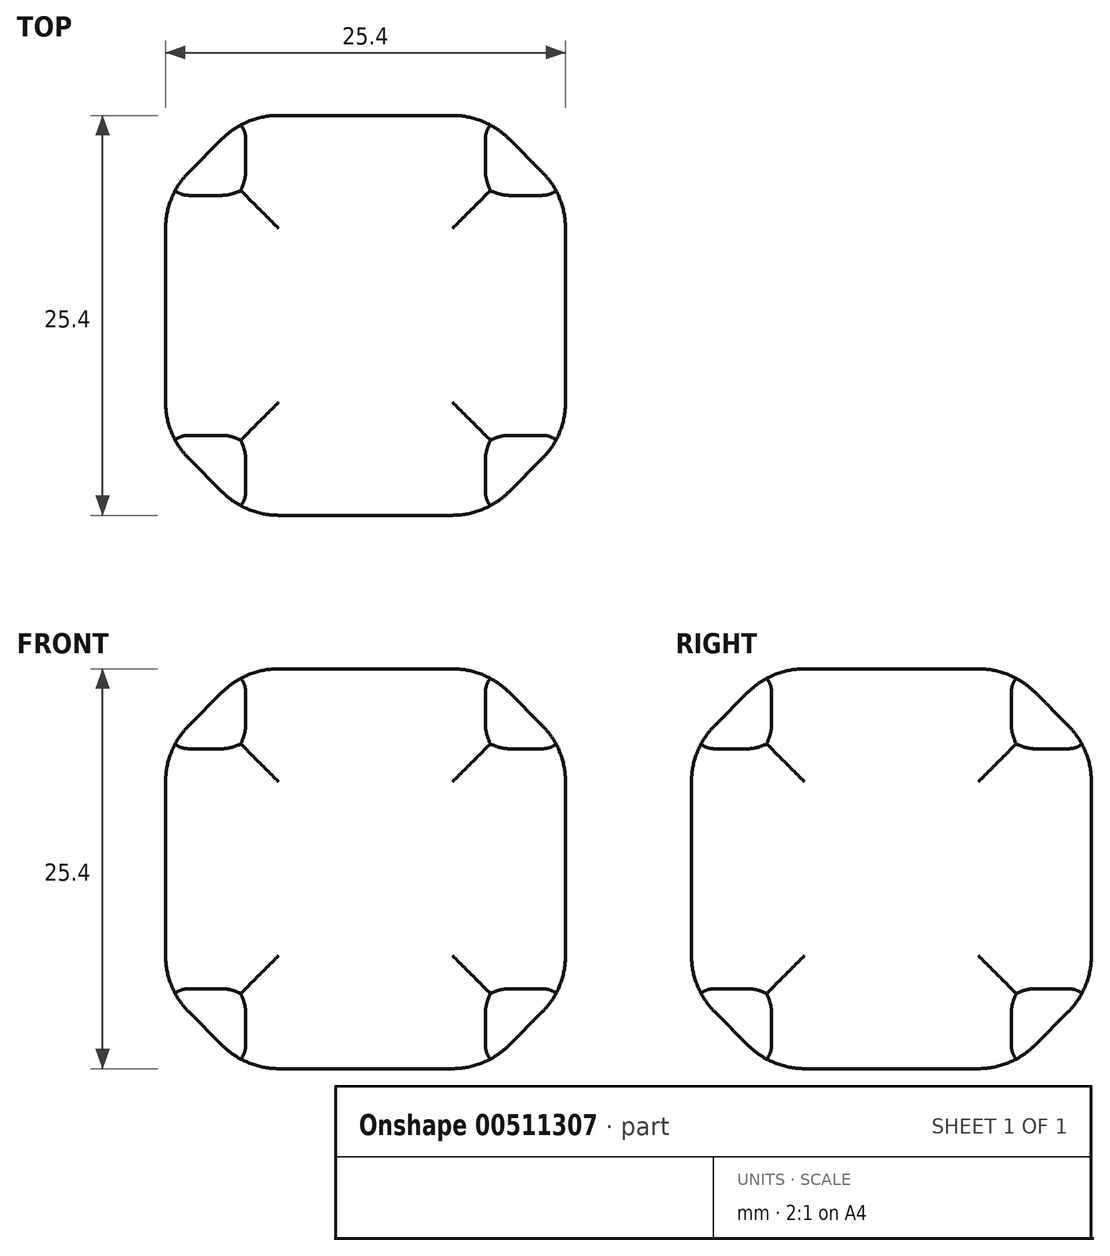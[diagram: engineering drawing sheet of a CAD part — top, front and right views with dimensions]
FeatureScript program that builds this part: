
annotation { "Feature Type Name" : "Feature", "Feature Type Description" : "" }
export const myFeature = defineFeature(function(context is Context, id is Id, definition is map)
    precondition{}
    {
        {
            var Q0;
            Q0=qCreatedBy(makeId("Front.planeOp"),FACE);
            var sketch = newSketch(context, id + "F0", { "sketchPlane" : qUnion([Q0])});
            skLineSegment(sketch, "E0.bottom", {"start": v(0, 0) * mm, "end": v(25.4, 0) * mm});
            skLineSegment(sketch, "E0.top", {"start": v(0, 25.4) * mm, "end": v(25.4, 25.4) * mm});
            skLineSegment(sketch, "E0.left", {"start": v(0, 0) * mm, "end": v(0, 25.4) * mm});
            skLineSegment(sketch, "E0.right", {"start": v(25.4, 0) * mm, "end": v(25.4, 25.4) * mm});
            skSolve(sketch);
        }
        {
            var Q0;
            Q0 = qSketchRegion(id + "F0", true);
            extrude(context, id + "F1", {"entities" : qUnion([Q0]), "depth" : 25.4 * mm, "offsetDistance" : 25.4 * mm});
        }
        {
            var Q0;
            Q0=makeQuery(id+"F1.opExtrude","SWEPT_EDGE",EDGE,{"disambiguationData":[OSD([sQuery(id+"F0.wireOp",EDGE,"E0.top"),sQuery(id+"F0.wireOp",EDGE,"E0.left")])]});
            var Q1;
            Q1=makeQuery(id+"F1.opExtrude","CAP_EDGE",EDGE,{"disambiguationData":[OSD([sQuery(id+"F0.wireOp",EDGE,"E0.left")])],"isStart":false});
            var Q2;
            Q2=makeQuery(id+"F1.opExtrude","CAP_EDGE",EDGE,{"disambiguationData":[OSD([sQuery(id+"F0.wireOp",EDGE,"E0.top")])],"isStart":false});
            var Q3;
            Q3=makeQuery(id+"F1.opExtrude","SWEPT_EDGE",EDGE,{"disambiguationData":[OSD([sQuery(id+"F0.wireOp",EDGE,"E0.bottom"),sQuery(id+"F0.wireOp",EDGE,"E0.left")])]});
            var Q4;
            Q4=makeQuery(id+"F1.opExtrude","CAP_EDGE",EDGE,{"disambiguationData":[OSD([sQuery(id+"F0.wireOp",EDGE,"E0.bottom")])],"isStart":false});
            var Q5;
            Q5=makeQuery(id+"F1.opExtrude","CAP_EDGE",EDGE,{"disambiguationData":[OSD([sQuery(id+"F0.wireOp",EDGE,"E0.left")])],"isStart":true});
            var Q6;
            Q6=makeQuery(id+"F1.opExtrude","CAP_EDGE",EDGE,{"disambiguationData":[OSD([sQuery(id+"F0.wireOp",EDGE,"E0.right")])],"isStart":false});
            var Q7;
            Q7=makeQuery(id+"F1.opExtrude","CAP_EDGE",EDGE,{"disambiguationData":[OSD([sQuery(id+"F0.wireOp",EDGE,"E0.right")])],"isStart":true});
            var Q8;
            Q8=makeQuery(id+"F1.opExtrude","SWEPT_EDGE",EDGE,{"disambiguationData":[OSD([sQuery(id+"F0.wireOp",EDGE,"E0.top"),sQuery(id+"F0.wireOp",EDGE,"E0.right")])]});
            var Q9;
            Q9=makeQuery(id+"F1.opExtrude","SWEPT_FACE",FACE,{"disambiguationData":[OSD([sQuery(id+"F0.wireOp",EDGE,"E0.right")])]});
            var Q10;
            Q10=makeQuery(id+"F1.opExtrude","CAP_EDGE",EDGE,{"disambiguationData":[OSD([sQuery(id+"F0.wireOp",EDGE,"E0.top")])],"isStart":true});
            var Q11;
            Q11=makeQuery(id+"F1.opExtrude","CAP_EDGE",EDGE,{"disambiguationData":[OSD([sQuery(id+"F0.wireOp",EDGE,"E0.bottom")])],"isStart":true});
            chamfer(context, id + "F2", {"entities" : qUnion([Q0, Q1, Q2, Q3, Q4, Q5, Q6, Q7, Q8, Q9, Q10, Q11]), "width" : 5.08 * mm, "tangentPropagation" : true});
        }
        {
            var Q0;
            {var subQ0=sQuery(id+"F0.wireOp",EDGE,"E0.top");Q0=makeQuery(id+"F2.opChamfer","BLEND_EDGE",EDGE,{"blendedFrom":[makeQuery(id+"F1.opExtrude","CAP_EDGE",EDGE,{"disambiguationData":[OSD([subQ0])],"isStart":false}),makeQuery(id+"F1.opExtrude","CAP_FACE",FACE,{"disambiguationData":[OSD([sQuery(id+"F0.wireOp",EDGE,"E0.bottom"),subQ0,sQuery(id+"F0.wireOp",EDGE,"E0.left"),sQuery(id+"F0.wireOp",EDGE,"E0.right")])],"isStart":false})],"blendedInto":[makeQuery(id+"F1.opExtrude","CAP_FACE",FACE,{"disambiguationData":[OSD([sQuery(id+"F0.wireOp",EDGE,"E0.bottom"),subQ0,sQuery(id+"F0.wireOp",EDGE,"E0.left"),sQuery(id+"F0.wireOp",EDGE,"E0.right")])],"isStart":false})]});}
            var Q1;
            {var subQ0=sQuery(id+"F0.wireOp",EDGE,"E0.left");Q1=makeQuery(id+"F2.opChamfer","BLEND_EDGE",EDGE,{"blendedFrom":[makeQuery(id+"F1.opExtrude","CAP_EDGE",EDGE,{"disambiguationData":[OSD([subQ0])],"isStart":false}),makeQuery(id+"F1.opExtrude","CAP_FACE",FACE,{"disambiguationData":[OSD([sQuery(id+"F0.wireOp",EDGE,"E0.bottom"),sQuery(id+"F0.wireOp",EDGE,"E0.top"),subQ0,sQuery(id+"F0.wireOp",EDGE,"E0.right")])],"isStart":false})],"blendedInto":[makeQuery(id+"F1.opExtrude","CAP_FACE",FACE,{"disambiguationData":[OSD([sQuery(id+"F0.wireOp",EDGE,"E0.bottom"),sQuery(id+"F0.wireOp",EDGE,"E0.top"),subQ0,sQuery(id+"F0.wireOp",EDGE,"E0.right")])],"isStart":false})]});}
            var Q2;
            {var subQ0=sQuery(id+"F0.wireOp",EDGE,"E0.bottom");Q2=makeQuery(id+"F2.opChamfer","BLEND_EDGE",EDGE,{"blendedFrom":[makeQuery(id+"F1.opExtrude","CAP_EDGE",EDGE,{"disambiguationData":[OSD([subQ0])],"isStart":false}),makeQuery(id+"F1.opExtrude","CAP_FACE",FACE,{"disambiguationData":[OSD([subQ0,sQuery(id+"F0.wireOp",EDGE,"E0.top"),sQuery(id+"F0.wireOp",EDGE,"E0.left"),sQuery(id+"F0.wireOp",EDGE,"E0.right")])],"isStart":false})],"blendedInto":[makeQuery(id+"F1.opExtrude","CAP_FACE",FACE,{"disambiguationData":[OSD([subQ0,sQuery(id+"F0.wireOp",EDGE,"E0.top"),sQuery(id+"F0.wireOp",EDGE,"E0.left"),sQuery(id+"F0.wireOp",EDGE,"E0.right")])],"isStart":false})]});}
            var Q3;
            {var subQ0=sQuery(id+"F0.wireOp",EDGE,"E0.right");Q3=makeQuery(id+"F2.opChamfer","BLEND_EDGE",EDGE,{"blendedFrom":[makeQuery(id+"F1.opExtrude","CAP_EDGE",EDGE,{"disambiguationData":[OSD([subQ0])],"isStart":false}),makeQuery(id+"F1.opExtrude","CAP_FACE",FACE,{"disambiguationData":[OSD([sQuery(id+"F0.wireOp",EDGE,"E0.bottom"),sQuery(id+"F0.wireOp",EDGE,"E0.top"),sQuery(id+"F0.wireOp",EDGE,"E0.left"),subQ0])],"isStart":false})],"blendedInto":[makeQuery(id+"F1.opExtrude","CAP_FACE",FACE,{"disambiguationData":[OSD([sQuery(id+"F0.wireOp",EDGE,"E0.bottom"),sQuery(id+"F0.wireOp",EDGE,"E0.top"),sQuery(id+"F0.wireOp",EDGE,"E0.left"),subQ0])],"isStart":false})]});}
            var Q4;
            {var subQ0=sQuery(id+"F0.wireOp",EDGE,"E0.left");Q4=makeQuery(id+"F2.opChamfer","BLEND_EDGE",EDGE,{"blendedFrom":[makeQuery(id+"F1.opExtrude","SWEPT_EDGE",EDGE,{"disambiguationData":[OSD([sQuery(id+"F0.wireOp",EDGE,"E0.top"),subQ0])]}),makeQuery(id+"F1.opExtrude","SWEPT_FACE",FACE,{"disambiguationData":[OSD([subQ0])]})],"blendedInto":[makeQuery(id+"F1.opExtrude","SWEPT_FACE",FACE,{"disambiguationData":[OSD([subQ0])]})]});}
            var Q5;
            {var subQ0=sQuery(id+"F0.wireOp",EDGE,"E0.left");Q5=makeQuery(id+"F2.opChamfer","BLEND_EDGE",EDGE,{"blendedFrom":[makeQuery(id+"F1.opExtrude","SWEPT_EDGE",EDGE,{"disambiguationData":[OSD([sQuery(id+"F0.wireOp",EDGE,"E0.bottom"),subQ0])]}),makeQuery(id+"F1.opExtrude","SWEPT_FACE",FACE,{"disambiguationData":[OSD([subQ0])]})],"blendedInto":[makeQuery(id+"F1.opExtrude","SWEPT_FACE",FACE,{"disambiguationData":[OSD([subQ0])]})]});}
            var Q6;
            {var subQ0=sQuery(id+"F0.wireOp",EDGE,"E0.left");Q6=makeQuery(id+"F2.opChamfer","BLEND_EDGE",EDGE,{"blendedFrom":[makeQuery(id+"F1.opExtrude","CAP_EDGE",EDGE,{"disambiguationData":[OSD([subQ0])],"isStart":true}),makeQuery(id+"F1.opExtrude","SWEPT_FACE",FACE,{"disambiguationData":[OSD([subQ0])]})],"blendedInto":[makeQuery(id+"F1.opExtrude","SWEPT_FACE",FACE,{"disambiguationData":[OSD([subQ0])]})]});}
            var Q7;
            {var subQ0=sQuery(id+"F0.wireOp",EDGE,"E0.left");Q7=makeQuery(id+"F2.opChamfer","BLEND_EDGE",EDGE,{"blendedFrom":[makeQuery(id+"F1.opExtrude","CAP_EDGE",EDGE,{"disambiguationData":[OSD([subQ0])],"isStart":false}),makeQuery(id+"F1.opExtrude","SWEPT_FACE",FACE,{"disambiguationData":[OSD([subQ0])]})],"blendedInto":[makeQuery(id+"F1.opExtrude","SWEPT_FACE",FACE,{"disambiguationData":[OSD([subQ0])]})]});}
            var Q8;
            {var subQ0=sQuery(id+"F0.wireOp",EDGE,"E0.top");Q8=makeQuery(id+"F2.opChamfer","BLEND_EDGE",EDGE,{"blendedFrom":[makeQuery(id+"F1.opExtrude","CAP_EDGE",EDGE,{"disambiguationData":[OSD([subQ0])],"isStart":true}),makeQuery(id+"F1.opExtrude","CAP_FACE",FACE,{"disambiguationData":[OSD([sQuery(id+"F0.wireOp",EDGE,"E0.bottom"),subQ0,sQuery(id+"F0.wireOp",EDGE,"E0.left"),sQuery(id+"F0.wireOp",EDGE,"E0.right")])],"isStart":true})],"blendedInto":[makeQuery(id+"F1.opExtrude","CAP_FACE",FACE,{"disambiguationData":[OSD([sQuery(id+"F0.wireOp",EDGE,"E0.bottom"),subQ0,sQuery(id+"F0.wireOp",EDGE,"E0.left"),sQuery(id+"F0.wireOp",EDGE,"E0.right")])],"isStart":true})]});}
            var Q9;
            {var subQ0=sQuery(id+"F0.wireOp",EDGE,"E0.right");Q9=makeQuery(id+"F2.opChamfer","BLEND_EDGE",EDGE,{"blendedFrom":[makeQuery(id+"F1.opExtrude","CAP_EDGE",EDGE,{"disambiguationData":[OSD([subQ0])],"isStart":true}),makeQuery(id+"F1.opExtrude","CAP_FACE",FACE,{"disambiguationData":[OSD([sQuery(id+"F0.wireOp",EDGE,"E0.bottom"),sQuery(id+"F0.wireOp",EDGE,"E0.top"),sQuery(id+"F0.wireOp",EDGE,"E0.left"),subQ0])],"isStart":true})],"blendedInto":[makeQuery(id+"F1.opExtrude","CAP_FACE",FACE,{"disambiguationData":[OSD([sQuery(id+"F0.wireOp",EDGE,"E0.bottom"),sQuery(id+"F0.wireOp",EDGE,"E0.top"),sQuery(id+"F0.wireOp",EDGE,"E0.left"),subQ0])],"isStart":true})]});}
            var Q10;
            {var subQ0=sQuery(id+"F0.wireOp",EDGE,"E0.bottom");Q10=makeQuery(id+"F2.opChamfer","BLEND_EDGE",EDGE,{"blendedFrom":[makeQuery(id+"F1.opExtrude","CAP_EDGE",EDGE,{"disambiguationData":[OSD([subQ0])],"isStart":true}),makeQuery(id+"F1.opExtrude","CAP_FACE",FACE,{"disambiguationData":[OSD([subQ0,sQuery(id+"F0.wireOp",EDGE,"E0.top"),sQuery(id+"F0.wireOp",EDGE,"E0.left"),sQuery(id+"F0.wireOp",EDGE,"E0.right")])],"isStart":true})],"blendedInto":[makeQuery(id+"F1.opExtrude","CAP_FACE",FACE,{"disambiguationData":[OSD([subQ0,sQuery(id+"F0.wireOp",EDGE,"E0.top"),sQuery(id+"F0.wireOp",EDGE,"E0.left"),sQuery(id+"F0.wireOp",EDGE,"E0.right")])],"isStart":true})]});}
            var Q11;
            {var subQ0=sQuery(id+"F0.wireOp",EDGE,"E0.left");Q11=makeQuery(id+"F2.opChamfer","BLEND_EDGE",EDGE,{"blendedFrom":[makeQuery(id+"F1.opExtrude","CAP_EDGE",EDGE,{"disambiguationData":[OSD([subQ0])],"isStart":true}),makeQuery(id+"F1.opExtrude","CAP_FACE",FACE,{"disambiguationData":[OSD([sQuery(id+"F0.wireOp",EDGE,"E0.bottom"),sQuery(id+"F0.wireOp",EDGE,"E0.top"),subQ0,sQuery(id+"F0.wireOp",EDGE,"E0.right")])],"isStart":true})],"blendedInto":[makeQuery(id+"F1.opExtrude","CAP_FACE",FACE,{"disambiguationData":[OSD([sQuery(id+"F0.wireOp",EDGE,"E0.bottom"),sQuery(id+"F0.wireOp",EDGE,"E0.top"),subQ0,sQuery(id+"F0.wireOp",EDGE,"E0.right")])],"isStart":true})]});}
            var Q12;
            {var subQ0=sQuery(id+"F0.wireOp",EDGE,"E0.right");Q12=makeQuery(id+"F2.opChamfer","BLEND_EDGE",EDGE,{"blendedFrom":[makeQuery(id+"F1.opExtrude","SWEPT_EDGE",EDGE,{"disambiguationData":[OSD([sQuery(id+"F0.wireOp",EDGE,"E0.top"),subQ0])]}),makeQuery(id+"F1.opExtrude","SWEPT_FACE",FACE,{"disambiguationData":[OSD([subQ0])]})],"blendedInto":[makeQuery(id+"F1.opExtrude","SWEPT_FACE",FACE,{"disambiguationData":[OSD([subQ0])]})]});}
            var Q13;
            {var subQ0=sQuery(id+"F0.wireOp",EDGE,"E0.right");Q13=makeQuery(id+"F2.opChamfer","BLEND_EDGE",EDGE,{"blendedFrom":[makeQuery(id+"F1.opExtrude","CAP_EDGE",EDGE,{"disambiguationData":[OSD([subQ0])],"isStart":false}),makeQuery(id+"F1.opExtrude","SWEPT_FACE",FACE,{"disambiguationData":[OSD([subQ0])]})],"blendedInto":[makeQuery(id+"F1.opExtrude","SWEPT_FACE",FACE,{"disambiguationData":[OSD([subQ0])]})]});}
            var Q14;
            {var subQ0=sQuery(id+"F0.wireOp",EDGE,"E0.right");Q14=makeQuery(id+"F2.opChamfer","BLEND_EDGE",EDGE,{"blendedFrom":[makeQuery(id+"F1.opExtrude","SWEPT_EDGE",EDGE,{"disambiguationData":[OSD([sQuery(id+"F0.wireOp",EDGE,"E0.bottom"),subQ0])]}),makeQuery(id+"F1.opExtrude","SWEPT_FACE",FACE,{"disambiguationData":[OSD([subQ0])]})],"blendedInto":[makeQuery(id+"F1.opExtrude","SWEPT_FACE",FACE,{"disambiguationData":[OSD([subQ0])]})]});}
            var Q15;
            {var subQ0=sQuery(id+"F0.wireOp",EDGE,"E0.right");Q15=makeQuery(id+"F2.opChamfer","BLEND_EDGE",EDGE,{"blendedFrom":[makeQuery(id+"F1.opExtrude","CAP_EDGE",EDGE,{"disambiguationData":[OSD([subQ0])],"isStart":true}),makeQuery(id+"F1.opExtrude","SWEPT_FACE",FACE,{"disambiguationData":[OSD([subQ0])]})],"blendedInto":[makeQuery(id+"F1.opExtrude","SWEPT_FACE",FACE,{"disambiguationData":[OSD([subQ0])]})]});}
            var Q16;
            {var subQ0=sQuery(id+"F0.wireOp",EDGE,"E0.bottom");Q16=makeQuery(id+"F2.opChamfer","BLEND_EDGE",EDGE,{"blendedFrom":[makeQuery(id+"F1.opExtrude","CAP_EDGE",EDGE,{"disambiguationData":[OSD([subQ0])],"isStart":false}),makeQuery(id+"F1.opExtrude","SWEPT_FACE",FACE,{"disambiguationData":[OSD([subQ0])]})],"blendedInto":[makeQuery(id+"F1.opExtrude","SWEPT_FACE",FACE,{"disambiguationData":[OSD([subQ0])]})]});}
            var Q17;
            {var subQ0=sQuery(id+"F0.wireOp",EDGE,"E0.bottom");Q17=makeQuery(id+"F2.opChamfer","BLEND_EDGE",EDGE,{"blendedFrom":[makeQuery(id+"F1.opExtrude","CAP_EDGE",EDGE,{"disambiguationData":[OSD([subQ0])],"isStart":true}),makeQuery(id+"F1.opExtrude","SWEPT_FACE",FACE,{"disambiguationData":[OSD([subQ0])]})],"blendedInto":[makeQuery(id+"F1.opExtrude","SWEPT_FACE",FACE,{"disambiguationData":[OSD([subQ0])]})]});}
            var Q18;
            {var subQ0=sQuery(id+"F0.wireOp",EDGE,"E0.bottom");Q18=makeQuery(id+"F2.opChamfer","BLEND_EDGE",EDGE,{"blendedFrom":[makeQuery(id+"F1.opExtrude","SWEPT_EDGE",EDGE,{"disambiguationData":[OSD([subQ0,sQuery(id+"F0.wireOp",EDGE,"E0.left")])]}),makeQuery(id+"F1.opExtrude","SWEPT_FACE",FACE,{"disambiguationData":[OSD([subQ0])]})],"blendedInto":[makeQuery(id+"F1.opExtrude","SWEPT_FACE",FACE,{"disambiguationData":[OSD([subQ0])]})]});}
            var Q19;
            {var subQ0=sQuery(id+"F0.wireOp",EDGE,"E0.bottom");Q19=makeQuery(id+"F2.opChamfer","BLEND_EDGE",EDGE,{"blendedFrom":[makeQuery(id+"F1.opExtrude","SWEPT_EDGE",EDGE,{"disambiguationData":[OSD([subQ0,sQuery(id+"F0.wireOp",EDGE,"E0.right")])]}),makeQuery(id+"F1.opExtrude","SWEPT_FACE",FACE,{"disambiguationData":[OSD([subQ0])]})],"blendedInto":[makeQuery(id+"F1.opExtrude","SWEPT_FACE",FACE,{"disambiguationData":[OSD([subQ0])]})]});}
            var Q20;
            {var subQ0=sQuery(id+"F0.wireOp",EDGE,"E0.top");Q20=makeQuery(id+"F2.opChamfer","BLEND_EDGE",EDGE,{"blendedFrom":[makeQuery(id+"F1.opExtrude","CAP_EDGE",EDGE,{"disambiguationData":[OSD([subQ0])],"isStart":false}),makeQuery(id+"F1.opExtrude","SWEPT_FACE",FACE,{"disambiguationData":[OSD([subQ0])]})],"blendedInto":[makeQuery(id+"F1.opExtrude","SWEPT_FACE",FACE,{"disambiguationData":[OSD([subQ0])]})]});}
            var Q21;
            {var subQ0=sQuery(id+"F0.wireOp",EDGE,"E0.top");Q21=makeQuery(id+"F2.opChamfer","BLEND_EDGE",EDGE,{"blendedFrom":[makeQuery(id+"F1.opExtrude","CAP_EDGE",EDGE,{"disambiguationData":[OSD([subQ0])],"isStart":true}),makeQuery(id+"F1.opExtrude","SWEPT_FACE",FACE,{"disambiguationData":[OSD([subQ0])]})],"blendedInto":[makeQuery(id+"F1.opExtrude","SWEPT_FACE",FACE,{"disambiguationData":[OSD([subQ0])]})]});}
            var Q22;
            {var subQ0=sQuery(id+"F0.wireOp",EDGE,"E0.top");Q22=makeQuery(id+"F2.opChamfer","BLEND_EDGE",EDGE,{"blendedFrom":[makeQuery(id+"F1.opExtrude","SWEPT_EDGE",EDGE,{"disambiguationData":[OSD([subQ0,sQuery(id+"F0.wireOp",EDGE,"E0.right")])]}),makeQuery(id+"F1.opExtrude","SWEPT_FACE",FACE,{"disambiguationData":[OSD([subQ0])]})],"blendedInto":[makeQuery(id+"F1.opExtrude","SWEPT_FACE",FACE,{"disambiguationData":[OSD([subQ0])]})]});}
            var Q23;
            {var subQ0=sQuery(id+"F0.wireOp",EDGE,"E0.top");Q23=makeQuery(id+"F2.opChamfer","BLEND_EDGE",EDGE,{"blendedFrom":[makeQuery(id+"F1.opExtrude","SWEPT_EDGE",EDGE,{"disambiguationData":[OSD([subQ0,sQuery(id+"F0.wireOp",EDGE,"E0.left")])]}),makeQuery(id+"F1.opExtrude","SWEPT_FACE",FACE,{"disambiguationData":[OSD([subQ0])]})],"blendedInto":[makeQuery(id+"F1.opExtrude","SWEPT_FACE",FACE,{"disambiguationData":[OSD([subQ0])]})]});}
            fillet(context, id + "F3", {"entities" : qUnion([Q0, Q1, Q2, Q3, Q4, Q5, Q6, Q7, Q8, Q9, Q10, Q11, Q12, Q13, Q14, Q15, Q16, Q17, Q18, Q19, Q20, Q21, Q22, Q23]), "radius" : 5.08 * mm, "tangentPropagation" : true, "allowEdgeOverflow" : false});
        }
    });
